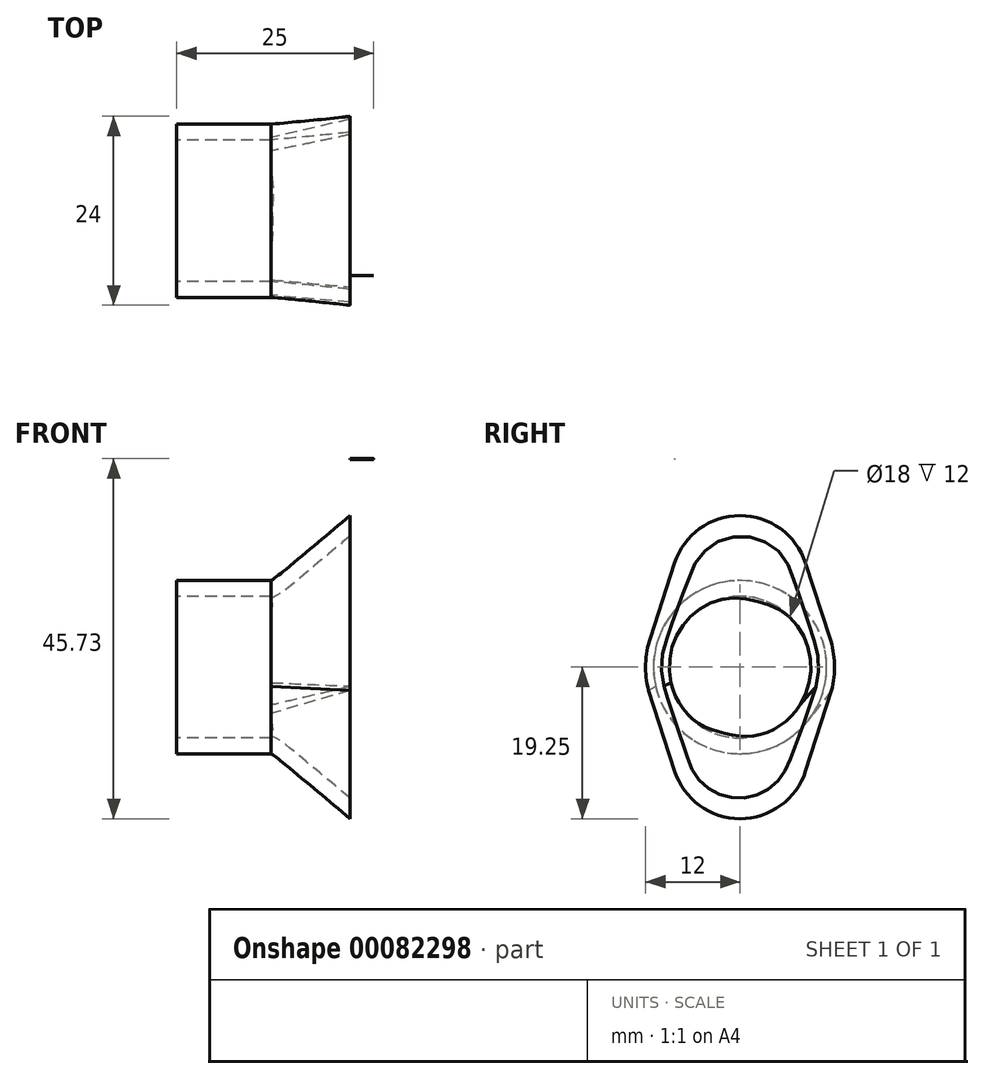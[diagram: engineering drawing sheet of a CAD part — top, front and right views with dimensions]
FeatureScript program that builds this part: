
annotation { "Feature Type Name" : "Feature", "Feature Type Description" : "" }
export const myFeature = defineFeature(function(context is Context, id is Id, definition is map)
    precondition{}
    {
        {
            var Q0;
            Q0=qCreatedBy(makeId("Right.planeOp"),FACE);
            cPlane(context, id + "F0", {"entities" : qUnion([Q0]), "cplaneType" : CPlaneType.OFFSET, "offset" : 10 * mm, "oppositeDirection" : true, "width" : 150 * mm, "height" : 150 * mm});
        }
        {
            var Q0;
            Q0=qCreatedBy(makeId("Right.planeOp"),FACE);
            var sketch = newSketch(context, id + "F1", { "sketchPlane" : qUnion([Q0])});
            skArc(sketch, "E0", {"start": v(-8.33, -13.19) * mm, "mid": v(0, -19.25) * mm, "end": v(8.33, -13.19) * mm});
            skArc(sketch, "E1", {"start": v(8.32, 13.2) * mm, "mid": v(0, 19.25) * mm, "end": v(-8.32, 13.2) * mm});
            skArc(sketch, "E2", {"start": v(11.17, -4.39) * mm, "mid": v(12, -0.36) * mm, "end": v(11.41, 3.71) * mm});
            skPoint(sketch, "E3.visualSharp", {"position": v(-8.5, -8.46) * mm});
            skPoint(sketch, "E4.visualSharp", {"position": v(8.5, -8.46) * mm});
            skArc(sketch, "E5.trimOffspring", {"start": v(-11.41, 3.71) * mm, "mid": v(-12, -0.36) * mm, "end": v(-11.17, -4.39) * mm});
            skPoint(sketch, "E6.visualSharp", {"position": v(-8.5, 8.46) * mm});
            skPoint(sketch, "E7.visualSharp", {"position": v(8.5, 8.46) * mm});
            skLineSegment(sketch, "E8", {"start": v(8.32, 13.2) * mm, "end": v(11.41, 3.71) * mm});
            skLineSegment(sketch, "E9", {"start": v(-8.32, 13.2) * mm, "end": v(-11.41, 3.71) * mm});
            skLineSegment(sketch, "E10", {"start": v(8.33, -13.19) * mm, "end": v(11.63, -2.97) * mm});
            skLineSegment(sketch, "E11", {"start": v(-8.33, -13.19) * mm, "end": v(-11.63, -2.97) * mm});
            skSolve(sketch);
        }
        {
            var Q0;
            Q0=qCreatedBy(id+"F0.planeOp",FACE);
            var sketch = newSketch(context, id + "F2", { "sketchPlane" : qUnion([Q0])});
            skCircle(sketch, "E12", {"center": v(0, 0) * mm, "radius": 11 * mm});
            skSolve(sketch);
        }
        {
            var Q0;
            Q0=makeQuery(id+"F1.imprint","IMPRINT",FACE,{"disambiguationData":[TD([[makeQuery(id+"F1.imprint","IMPRINT",EDGE,{"derivedFrom":sQuery(id+"F1.wireOp",EDGE,"E0")}),1.0]])]});
            var Q1;
            Q1=makeQuery(id+"F2.imprint","IMPRINT",FACE,{"disambiguationData":[TD([[makeQuery(id+"F2.imprint","IMPRINT",EDGE,{"derivedFrom":sQuery(id+"F2.wireOp",EDGE,"E12")}),1.0]])]});
            loft(context, id + "F3", {"sheetProfilesArray" : [{ "sheetProfileEntities" : qUnion([Q0]) }, { "sheetProfileEntities" : qUnion([Q1]) }]});
        }
        {
            var Q0;
            Q0=makeQuery(id+"F3.opLoft","CAP_FACE",FACE,{"disambiguationData":[OSD([makeQuery(id+"F2.imprint","IMPRINT",FACE,{"disambiguationData":[TD([[makeQuery(id+"F2.imprint","IMPRINT",EDGE,{"derivedFrom":sQuery(id+"F2.wireOp",EDGE,"E12")}),1.0]])]})])],"isStart":true});
            var Q1;
            Q1=makeQuery(id+"F3.opLoft","CAP_FACE",FACE,{"disambiguationData":[OSD([makeQuery(id+"F1.imprint","IMPRINT",FACE,{"disambiguationData":[TD([[makeQuery(id+"F1.imprint","IMPRINT",EDGE,{"derivedFrom":sQuery(id+"F1.wireOp",EDGE,"E0")}),1.0]])]})])],"isStart":true});
            shell(context, id + "F4", {"entities" : qUnion([Q0, Q1]), "thickness" : 2 * mm});
        }
        {
            var Q0;
            Q0=makeQuery(id+"F2.imprint","IMPRINT",FACE,{"disambiguationData":[TD([[makeQuery(id+"F2.imprint","IMPRINT",EDGE,{"derivedFrom":sQuery(id+"F2.wireOp",EDGE,"E12")}),1.0]])]});
            extrude(context, id + "F5", {"entities" : qUnion([Q0]), "operationType" : NewBodyOperationType.ADD, "oppositeDirection" : true, "depth" : 12 * mm, "offsetDistance" : 25 * mm});
        }
        {
            var Q0;
            Q0=makeQuery(id+"F5.opExtrude","CAP_FACE",FACE,{"disambiguationData":[OSD([sQuery(id+"F2.wireOp",EDGE,"E12")])],"isStart":false});
            var sketch = newSketch(context, id + "F6", { "sketchPlane" : qUnion([Q0])});
            skPoint(sketch, "E13", {"position": v(0, 0) * mm});
            skSolve(sketch);
        }
        {
            var Q0;
            Q0=sQuery(id+"F6.wireOp",VERTEX,"E13");
            var Q1;
            Q1=makeQuery(id+"F3.opLoft","SWEPT_BODY",BODY,{"disambiguationData":[OSD([makeQuery(id+"F1.imprint","IMPRINT",FACE,{"disambiguationData":[TD([[makeQuery(id+"F1.imprint","IMPRINT",EDGE,{"derivedFrom":sQuery(id+"F1.wireOp",EDGE,"E0")}),1.0]])]}),makeQuery(id+"F2.imprint","IMPRINT",FACE,{"disambiguationData":[TD([[makeQuery(id+"F2.imprint","IMPRINT",EDGE,{"derivedFrom":sQuery(id+"F2.wireOp",EDGE,"E12")}),1.0]])]})])]});
            hole(context, id + "F7", {"style" : HoleStyle.SIMPLE, "endStyle" : HoleEndStyle.BLIND, "holeDiameter" : 18 * mm, "majorDiameter" : 5 * mm, "holeDepth" : 12 * mm, "isTappedThrough" : true, "tappedDepth" : 12 * mm, "tapClearance" : 3, "startFromSketch" : true, "locations" : qUnion([Q0]), "scope" : qUnion([Q1])});
        }
        {
            var Q0;
            Q0=qCreatedBy(makeId("Right.planeOp"),FACE);
            var sketch = newSketch(context, id + "F8", { "sketchPlane" : qUnion([Q0])});
            skArc(sketch, "E14", {"start": v(8.25, 26.48) * mm, "mid": v(-0.04, 34.73) * mm, "end": v(-8.25, 26.4) * mm});
            skArc(sketch, "E15", {"start": v(-8.25, -25.27) * mm, "mid": v(0, -33.52) * mm, "end": v(8.25, -25.27) * mm});
            skCircle(sketch, "E16", {"center": v(0, 26.48) * mm, "radius": 2.25 * mm});
            skCircle(sketch, "E17", {"center": v(0, -25.27) * mm, "radius": 2.25 * mm});
            skPoint(sketch, "E18.end.orphan", {"position": v(8.25, -25.27) * mm});
            skPoint(sketch, "E18.start.orphan", {"position": v(8.25, 26.48) * mm});
            skPoint(sketch, "E19.end.orphan", {"position": v(-8.25, -25.27) * mm});
            skPoint(sketch, "E19.start.orphan", {"position": v(-8.25, 26.48) * mm});
            skLineSegment(sketch, "E20", {"start": v(8.25, -25.27) * mm, "end": v(8.25, -14.2) * mm});
            skLineSegment(sketch, "E21", {"start": v(8.25, 26.48) * mm, "end": v(8.25, 14.2) * mm});
            skLineSegment(sketch, "E22", {"start": v(-8.25, 26.4) * mm, "end": v(-8.25, 26.48) * mm});
            skArc(sketch, "E23", {"start": v(-11.36, 3.88) * mm, "mid": v(-12, -0.27) * mm, "end": v(-11.17, -4.39) * mm});
            skLineSegment(sketch, "E24", {"start": v(-8.25, 26.4) * mm, "end": v(-8.25, 14.2) * mm});
            skPoint(sketch, "E25.orphan", {"position": v(-8.25, -11.06) * mm});
            skArc(sketch, "E26.trimOffspring", {"start": v(11.25, -4.18) * mm, "mid": v(12, -0.21) * mm, "end": v(11.39, 3.78) * mm});
            skPoint(sketch, "E27.visualSharp", {"position": v(-8.25, 8.71) * mm});
            skPoint(sketch, "E28.visualSharp", {"position": v(8.25, 8.71) * mm});
            skPoint(sketch, "E29.visualSharp", {"position": v(8.25, -8.71) * mm});
            skPoint(sketch, "E30.visualSharp", {"position": v(-8.25, -8.71) * mm});
            skArc(sketch, "E31", {"start": v(-6.99, 5.67) * mm, "mid": v(-9, -0.1) * mm, "end": v(-6.85, -5.84) * mm});
            skArc(sketch, "E32", {"start": v(5.93, 9.58) * mm, "mid": v(0, 16.5) * mm, "end": v(-5.93, 9.58) * mm});
            skArc(sketch, "E33", {"start": v(-5.7, -9.74) * mm, "mid": v(0, -16.25) * mm, "end": v(5.7, -9.74) * mm});
            skArc(sketch, "E34.trimOffspring", {"start": v(6.85, -5.84) * mm, "mid": v(9, -0.1) * mm, "end": v(6.99, 5.67) * mm});
            skPoint(sketch, "E35.visualSharp", {"position": v(-4.93, -7.53) * mm});
            skArc(sketch, "E35.filletArc", {"start": v(-5.7, -9.74) * mm, "mid": v(-5.86, -7.67) * mm, "end": v(-6.85, -5.84) * mm});
            skPoint(sketch, "E36.visualSharp", {"position": v(4.93, -7.53) * mm});
            skArc(sketch, "E36.filletArc", {"start": v(6.85, -5.84) * mm, "mid": v(5.86, -7.67) * mm, "end": v(5.7, -9.74) * mm});
            skPoint(sketch, "E37.visualSharp", {"position": v(5.13, 7.4) * mm});
            skArc(sketch, "E37.filletArc", {"start": v(5.93, 9.58) * mm, "mid": v(6.04, 7.52) * mm, "end": v(6.99, 5.67) * mm});
            skPoint(sketch, "E38.visualSharp", {"position": v(-5.13, 7.4) * mm});
            skArc(sketch, "E38.filletArc", {"start": v(-6.99, 5.67) * mm, "mid": v(-6.04, 7.52) * mm, "end": v(-5.93, 9.58) * mm});
            skLineSegment(sketch, "E39", {"start": v(-8.5, -12.66) * mm, "end": v(-11.17, -4.39) * mm});
            skLineSegment(sketch, "E40", {"start": v(11.25, -4.18) * mm, "end": v(11.25, -4.18) * mm});
            skLineSegment(sketch, "E41", {"start": v(11.26, -4.15) * mm, "end": v(8.5, -12.64) * mm});
            skLineSegment(sketch, "E42", {"start": v(11.43, 3.66) * mm, "end": v(8.5, 12.65) * mm});
            skLineSegment(sketch, "E43", {"start": v(-11.36, 3.88) * mm, "end": v(-8.5, 12.64) * mm});
            skLineSegment(sketch, "E44.trimOffspring", {"start": v(-8.25, -14.2) * mm, "end": v(-8.25, -25.27) * mm});
            skPoint(sketch, "E45.visualSharp", {"position": v(-8.25, -13.41) * mm});
            skArc(sketch, "E45.filletArc", {"start": v(-8.25, -14.2) * mm, "mid": v(-8.31, -13.42) * mm, "end": v(-8.5, -12.66) * mm});
            skPoint(sketch, "E46.visualSharp", {"position": v(8.25, -13.4) * mm});
            skArc(sketch, "E46.filletArc", {"start": v(8.5, -12.64) * mm, "mid": v(8.31, -13.4) * mm, "end": v(8.25, -14.2) * mm});
            skPoint(sketch, "E47.visualSharp", {"position": v(8.25, 13.4) * mm});
            skArc(sketch, "E47.filletArc", {"start": v(8.25, 14.2) * mm, "mid": v(8.31, 13.41) * mm, "end": v(8.5, 12.65) * mm});
            skPoint(sketch, "E48.visualSharp", {"position": v(-8.25, 13.4) * mm});
            skArc(sketch, "E48.filletArc", {"start": v(-8.5, 12.64) * mm, "mid": v(-8.31, 13.41) * mm, "end": v(-8.25, 14.2) * mm});
            skSolve(sketch);
        }
        {
            var Q0;
            Q0=makeQuery(id+"F8.imprint","IMPRINT",FACE,{"disambiguationData":[TD([[makeQuery(id+"F8.imprint","IMPRINT",EDGE,{"derivedFrom":sQuery(id+"F8.wireOp",EDGE,"E14")}),1.0]])]});
            extrude(context, id + "F9", {"entities" : qUnion([Q0]), "operationType" : NewBodyOperationType.ADD, "depth" : 3 * mm, "offsetDistance" : 25 * mm});
        }
    });
